# Revit family: PRD_AR_TltRllHldrs_STRATOS_DoubleToiletRollHolder_STRX671,STRX671L,STRX672
name_source: partatom
category: Specialty Equipment
revit_build: Autodesk Revit 2018 (Build: 20190510_1515(x64)
units: mm (PartAtom-declared; Revit-internal decimal feet)

## family parameters
Cut with Voids When Loaded = No
Host = Face
OmniClass Number = 23.40.20.21.21
OmniClass Title = Toilet Paper Dispensers
Part Type = Normal
Room Calculation Point = No
Round Connector Dimension = Use Diameter
Shared = No

## types (3) — shared parameters
AssetType = Fixed
Category = Pr_40_20_76_88, Toilet roll holders
Color = Stainless steel
Default Elevation = 700 mm  [stored 2.29659 ft]
DurationUnit = year
FillingQuantity = 2 Rolls
Finish = Satin finished
FinishAndColour = Stainless steel, satin finished
Form = Wall mounting
IfcExportAs = IfcFurnitureType
IfcExportType = NOTDEFINED
IntegralAccessories = incl. stainless steel screws and dowels
Lock = key-lock
MainColor = Stainless steel
Manufacturer = KWC Group AG
ManufacturerName = KWC Group AG
ManufacturerURL = www.kwc.com
Material = Stainless steel
Materials = Stainless steel
NBSDescription = Toilet roll holders
NBSReference = 45-35-72/368
ProductInformation = https://pim.kwc.com
RollHolderMaterial = PRD_AR_StainlessSteel_SatinFinished
Style = Toilet roll holder
SurfaceTreatment = InoxPlus (anti fingerprint)
ToiletRollMaterial = PRD_AR_ToiletRoll
URL = www.kwc.com
Uniclass2015Code = Pr_40_20_76_88
Uniclass2015Title = Toilet roll holders
Uniclass2015Version = Products v1.7
Version = 1
WarrantyDurationUnit = year

## per-type parameters (varying)
| type | BIMObjectName | Description | Features | GrossWeight | MaximumWidthOfConsumable | Model | ModelNumber | ModelReference | Name | NetWeight | NominalDepth | NominalHeight | NominalLength | NominalWidth | Size | Type |
| STRX672 with spindle system | PRD_AR_ToiletRollHolders_STRATOS_DoubleToiletRollHolder_STRX672 | Double toilet roll holder with spindle system for wall mounting, stainless steel, surface satin finished, front with InoxPlus surface refinement for the reduction of finger marks and better cleaning characteristics (easy to clean), material thickness 1.5 mm, curved front cover, cylinder lock with KWC standard key, for 2 rolls with max. ⌀120 mm, second roll will be released after consumption of first roll, with spindles, reserve roll not visible, incl. stainless steel screws and dowels. | stainless steel, 1.50 mm, wall mounting, 156x303x141 mm (WxHxD) | 3.20 kg | 100 mm  [stored 0.328084 ft] | STRX672 | 2000057399 | STRX672 | STRATOS Double toilet roll holder STRX672 | 2.76 kg | 141 mm | 303 mm  [stored 0.994094 ft] | 156 mm  [stored 0.511811 ft] | 156 mm  [stored 0.511811 ft] | 156x303x141 mm | STRX672 |
| STRX671 without spindle system | PRD_AR_ToiletRollHolders_STRATOS_DoubleToiletRollHolder_STRX671 | Double toilet roll holder for wall mounting, stainless steel, surface satin finished, front with InoxPlus surface refinement for the reduction of finger marks and better cleaning characteristics (easy to clean), material thickness 1.5 mm, curved front cover, cylinder lock with KWC standard key, for 2 rolls with max. Ø 120 mm, second roll will be released after consumption of first roll, without spindles, incl. stainless steel screws and dowels. | stainless steel, 1.50 mm, wall mounting, 156x305x141 mm (WxHxD) | 3.03 kg | 100 mm  [stored 0.328084 ft] | STRX671 | 2000057395 | STRX671 | STRATOS Double toilet roll holder STRX671 | 2.76 kg | 141 mm | 305 mm  [stored 1.00066 ft] | 156 mm  [stored 0.511811 ft] | 156 mm  [stored 0.511811 ft] | 156x305x141 mm | STRX671 |
| STRX671L without spindle system | PRD_AR_ToiletRollHolders_STRATOS_DoubleToiletRollHolder_STRX671L | Double toilet roll holder without spindle system for wall mounting, stainless steel, surface satin finished, front with InoxPlus surface refinement for the reduction of finger marks and better cleaning characteristics (easy to clean), material thickness 1.5 mm, curved front cover, cylinder lock with KWC standard key, for 2 rolls with max. Ø 140 mm, second roll will be released after consumption of first roll, incl. stainless steel screws and dowels. | stainless steel, 1.50 mm, wall mounting, 170x343x166 mm (WxHxD) | 4.19 kg | 115 mm  [stored 0.377297 ft] | STRX671L | 2000057397 | STRX671L | STRATOS Double toilet roll holder STRX671L | 3.67 kg | 166 mm  [stored 0.544619 ft] | 343 mm  [stored 1.12533 ft] | 170 mm  [stored 0.557743 ft] | 170 mm  [stored 0.557743 ft] | 170x343x166 mm | STRX671L |

note: [stored X ft] marks values corroborated as IEEE doubles in the binary element streams (Revit-internal decimal feet)

## geometry (parser evidence)
native form markers: Sweep x2
no freeform markers — native parametric forms only
